# Revit family: Casement_38_C_Top_Hung_Standard
name_source: partatom
category: Windows
revit_build: Autodesk Revit 2014 (Build: 20130308_1515(x64)
units: mm (PartAtom-declared; Revit-internal decimal feet)

## types (6) — shared parameters
Aluminium Thickness = 1 mm  [stored 0.00328084 ft]
Area Pane Left = 0.22 m²
Area Pane Right = 0.22 m²
Bead SG Gap = 13 mm  [stored 0.0426509 ft]
Bottom Hung = No
Casement Dimension = 38 mm  [stored 0.124672 ft]
Custom Sash Left Width = 554 mm  [stored 1.81759 ft]
Custom Sash Right Width = 554 mm  [stored 1.81759 ft]
Custom Window Height = 590 mm  [stored 1.9357 ft]
DG Extrusion Start = 9 mm  [stored 0.0295276 ft]
DG Gasket Finish = Double Glazing Gasket Material
DG Thickness Calc = 4 mm  [stored 0.0131234 ft]
Default Sill Height = 800 mm  [stored 2.62467 ft]
Depth Bead = 24 mm  [stored 0.0787402 ft]
Depth Mullion = 39 mm  [stored 0.127953 ft]
Description = Window 38mm, Type C top hung
Frame Center Offset = 19 mm  [stored 0.062336 ft]
Height = 590 mm  [stored 1.9357 ft]
Height Fixed Panel Center = 530 mm  [stored 1.73885 ft]
Height Sash = 514 mm
Height Sash Opening = 544 mm  [stored 1.78478 ft]
Length Mullion = 590 mm  [stored 1.9357 ft]
Limit Fixed Pane Width Max = 1500 mm  [stored 4.92126 ft]
Limit Fixed Pane Width Min = 200 mm  [stored 0.656168 ft]
Limit Sash Height Max = 1200 mm
Limit Sash Height Min = 300 mm  [stored 0.984252 ft]
Limit Sash Width Max = 1500 mm  [stored 4.92126 ft]
Limit Sash Width Min = 300 mm  [stored 0.984252 ft]
Limit Window Height Max = 1246 mm  [stored 4.08793 ft]
Limit Window Height Min = 346 mm
Limit Window Width Max = 2700 mm
Limit Window Width Min = 1400 mm
Manufacturer = Crealco
Max System DG One Piece Thickness = 6 mm  [stored 0.019685 ft]
Max System DG Unit Thickness = 25 mm  [stored 0.082021 ft]
Model = Casement 38
Mullion Depth Windload Based = 39 mm  [stored 0.127953 ft]
Offset Bead Center Reversed = 19 mm  [stored 0.062336 ft]
Offset Fixed Panel Left = 600 mm  [stored 1.9685 ft]
Offset Mullion Left Side = 570 mm  [stored 1.87008 ft]
Offset Mullion Right Side = 570 mm  [stored 1.87008 ft]
Offset Sash Side = 23 mm  [stored 0.0754593 ft]
Offset Sash Top = 23 mm  [stored 0.0754593 ft]
Offset Window Exterior = 19 mm  [stored 0.062336 ft]
SG Gasket Thickness = 6 mm  [stored 0.019685 ft]
Sash Center Offset = 16 mm  [stored 0.0524934 ft]
Sash Height = 545 mm  [stored 1.78806 ft]
Sash Overlap = 7 mm  [stored 0.0229659 ft]
Sash Spacing Inner = 8 mm  [stored 0.0262467 ft]
Top Hung = Yes
URL = http://www.crealco.co.za
Wall Closure = By host
Width Bead = 15 mm  [stored 0.0492126 ft]
Width Profile = 30 mm  [stored 0.0984252 ft]
Width Sash Left = 554 mm  [stored 1.81759 ft]
Width Sash Left Opening = 524 mm  [stored 1.71916 ft]
Width Sash Right = 554 mm  [stored 1.81759 ft]
Width Sash Right Opening = 524 mm  [stored 1.71916 ft]
zero-valued in all types: Window Exterior Offset

## per-type parameters (varying)
| type | Area Pane Middle | Clearvue Insulated LowE SHGC Value | Clearvue Insulated LowE U Value | Clearvue Insulated SHGC Value | Clearvue Insulated U Value | Clearvue SHGC Value | Clearvue U Value | Custom Windload | Custom Window Width | Energy Advantage SHGC Value | Energy Advantage U Value | Intruderprufe Insulated LowE SHGC Value | Intruderprufe Insulated LowE U Value | Intruderprufe Insulated SHGC Value | Intruderprufe Insulated U Value | Intruderprufe LowE SHGC Value | Intruderprufe LowE U Value | Intruderprufe SHGC Value | Intruderprufe U Value | Max Pane Area | Width | Width Fixed Panel Center | Windload Design |
| 38-1806TT-1000Pa | 0.3 m² | 0.455 | 3.77 | 0.499 | 4.23 | 0.57 | 6.26 | 1000 mm  [stored 3.28084 ft] | 1790 mm  [stored 5.8727 ft] | 0.512 | 4.85 | 0.422 | 3.68 | 0.462 | 4.13 | 0.481 | 4.73 | 0.554 | 6.12 | 0.3 m² | 1790 mm  [stored 5.8727 ft] | 590 mm  [stored 1.9357 ft] | 1000 mm  [stored 3.28084 ft] |
| 38-1806TT-1500Pa | 0.3 m² | 0.455 | 3.77 | 0.499 | 4.23 | 0.57 | 6.26 | 1500 mm  [stored 4.92126 ft] | 1790 mm  [stored 5.8727 ft] | 0.512 | 4.85 | 0.422 | 3.68 | 0.462 | 4.13 | 0.481 | 4.73 | 0.554 | 6.12 | 0.3 m² | 1790 mm  [stored 5.8727 ft] | 590 mm  [stored 1.9357 ft] | 1500 mm  [stored 4.92126 ft] |
| 38-1806TT-2000Pa | 0.3 m² | 0.455 | 3.77 | 0.499 | 4.23 | 0.57 | 6.26 | 2000 mm  [stored 6.56168 ft] | 1790 mm  [stored 5.8727 ft] | 0.512 | 4.85 | 0.422 | 3.68 | 0.462 | 4.13 | 0.481 | 4.73 | 0.554 | 6.12 | 0.3 m² | 1790 mm  [stored 5.8727 ft] | 590 mm  [stored 1.9357 ft] | 2000 mm  [stored 6.56168 ft] |
| 38-2406TT-1000Pa | 0.61 m² | 0.485 | 3.52 | 0.532 | 4.03 | 0.608 | 6.19 | 1000 mm  [stored 3.28084 ft] | 2390 mm  [stored 7.84121 ft] | 0.545 | 4.69 | 0.449 | 3.45 | 0.494 | 3.94 | 0.511 | 4.57 | 0.585 | 6.06 | 0.61 m² | 2390 mm  [stored 7.84121 ft] | 1190 mm  [stored 3.9042 ft] | 1000 mm  [stored 3.28084 ft] |
| 38-2406TT-1500Pa | 0.61 m² | 0.485 | 3.52 | 0.532 | 4.03 | 0.608 | 6.19 | 1500 mm  [stored 4.92126 ft] | 2390 mm  [stored 7.84121 ft] | 0.545 | 4.69 | 0.449 | 3.45 | 0.494 | 3.94 | 0.511 | 4.57 | 0.585 | 6.06 | 0.61 m² | 2390 mm  [stored 7.84121 ft] | 1190 mm  [stored 3.9042 ft] | 1500 mm  [stored 4.92126 ft] |
| 38-2406TT-2000Pa | 0.61 m² | 0.485 | 3.52 | 0.532 | 4.03 | 0.608 | 6.19 | 2000 mm  [stored 6.56168 ft] | 2390 mm  [stored 7.84121 ft] | 0.545 | 4.69 | 0.449 | 3.45 | 0.494 | 3.94 | 0.511 | 4.57 | 0.585 | 6.06 | 0.61 m² | 2390 mm  [stored 7.84121 ft] | 1190 mm  [stored 3.9042 ft] | 2000 mm  [stored 6.56168 ft] |

note: [stored X ft] marks values corroborated as IEEE doubles in the binary element streams (Revit-internal decimal feet)

## geometry (parser evidence)
native form markers: Extrusion x1, Sweep x29
no freeform markers — native parametric forms only
